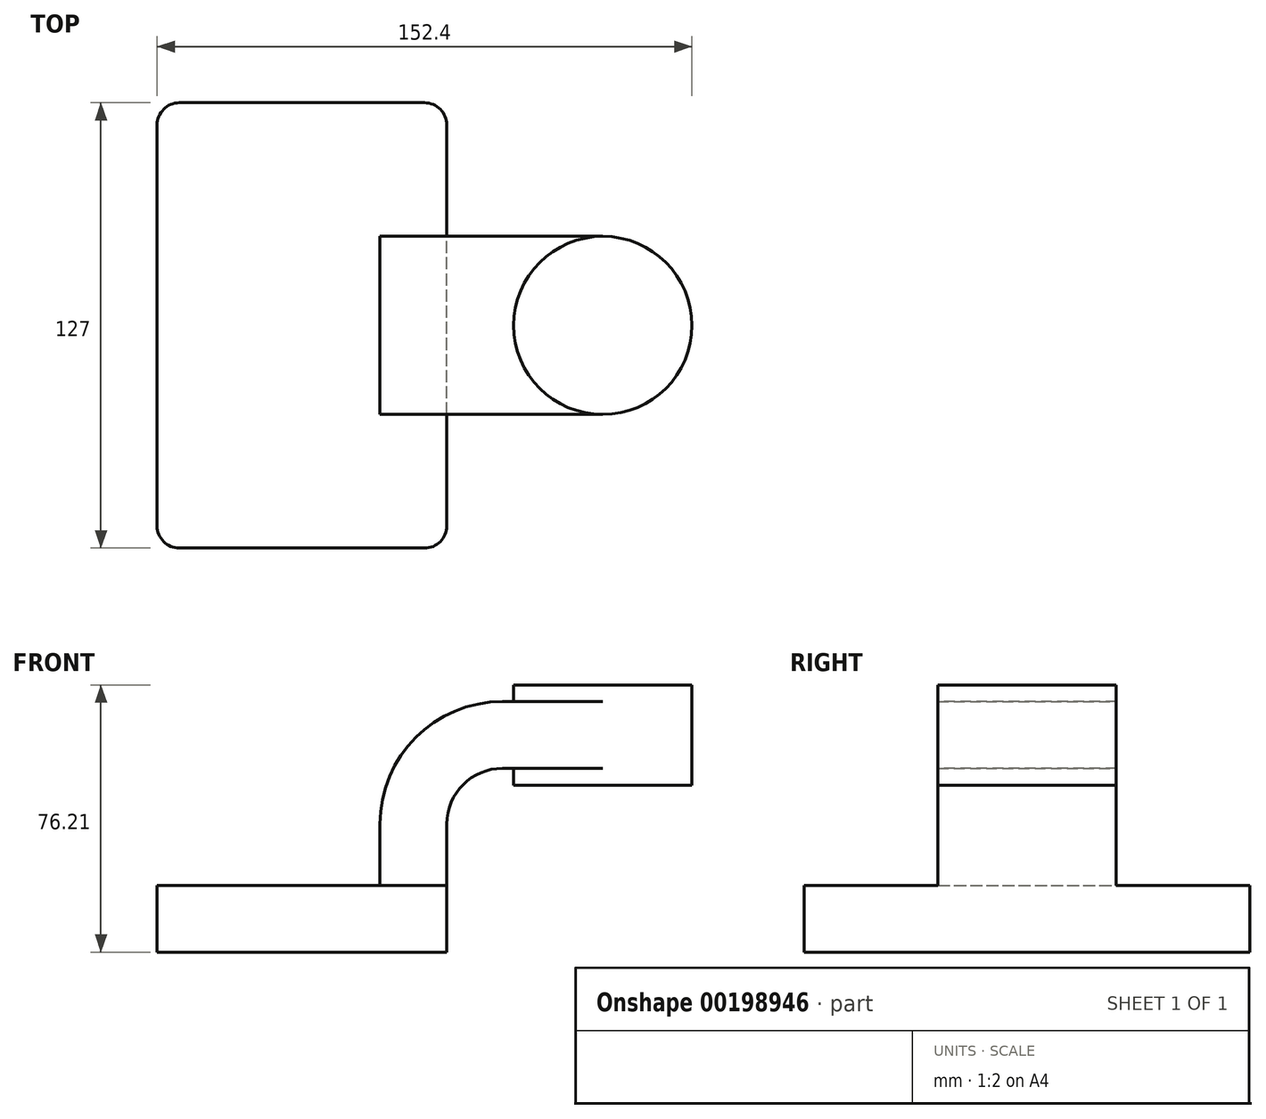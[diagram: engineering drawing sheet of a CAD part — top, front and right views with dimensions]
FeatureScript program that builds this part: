
annotation { "Feature Type Name" : "Feature", "Feature Type Description" : "" }
export const myFeature = defineFeature(function(context is Context, id is Id, definition is map)
    precondition{}
    {
        {
            var Q0;
            Q0=qCreatedBy(makeId("Front.planeOp"),FACE);
            var sketch = newSketch(context, id + "F0", { "sketchPlane" : qUnion([Q0])});
            skLineSegment(sketch, "E0.bottom", {"start": v(-41.28, 9.52) * mm, "end": v(41.28, 9.53) * mm});
            skLineSegment(sketch, "E0.top", {"start": v(-41.28, -9.53) * mm, "end": v(41.28, -9.53) * mm});
            skLineSegment(sketch, "E0.left", {"start": v(-41.28, 9.52) * mm, "end": v(-41.28, -9.53) * mm});
            skLineSegment(sketch, "E0.right", {"start": v(41.28, 9.53) * mm, "end": v(41.28, -9.52) * mm});
            skPoint(sketch, "E0.middle", {"position": v(0, 0) * mm});
            skLineSegment(sketch, "E1.bottom", {"start": v(60.33, 66.67) * mm, "end": v(111.12, 66.67) * mm});
            skLineSegment(sketch, "E1.top", {"start": v(60.33, 38.1) * mm, "end": v(111.12, 38.1) * mm});
            skLineSegment(sketch, "E1.left", {"start": v(60.33, 66.68) * mm, "end": v(60.33, 38.1) * mm});
            skLineSegment(sketch, "E1.right", {"start": v(111.12, 66.67) * mm, "end": v(111.12, 38.1) * mm});
            skPoint(sketch, "E1.middle", {"position": v(85.73, 52.39) * mm});
            skLineSegment(sketch, "E2", {"start": v(41.27, 9.53) * mm, "end": v(41.27, 27) * mm});
            skArc(sketch, "E3", {"start": v(41.27, 27) * mm, "mid": v(45.92, 38.23) * mm, "end": v(57.15, 42.88) * mm});
            skLineSegment(sketch, "E4", {"start": v(57.15, 42.88) * mm, "end": v(85.73, 42.88) * mm});
            skLineSegment(sketch, "E5.0", {"start": v(57.15, 61.93) * mm, "end": v(85.73, 61.93) * mm});
            skArc(sketch, "E5.1", {"start": v(22.22, 27) * mm, "mid": v(32.45, 51.7) * mm, "end": v(57.15, 61.93) * mm});
            skLineSegment(sketch, "E5.2", {"start": v(22.23, 9.53) * mm, "end": v(22.23, 27) * mm});
            skLineSegment(sketch, "E6", {"start": v(85.73, 66.67) * mm, "end": v(85.73, 38.1) * mm});
            skFitSpline(sketch, "E7", {"points": [v(-41.28, 9.52) * mm, v(57.15, 61.93) * mm], "startDerivative": vector(6.55, 94.18) * mm, "endDerivative": vector(106.57, 0) * mm});
            skSolve(sketch);
        }
        {
            var Q0;
            Q0=makeQuery(id+"F0.imprint","IMPRINT",FACE,{"disambiguationData":[TD([[makeQuery(id+"F0.imprint","IMPRINT",EDGE,{"derivedFrom":sQuery(id+"F0.wireOp",EDGE,"E0.top")}),1.0]])]});
            extrude(context, id + "F1", {"entities" : qUnion([Q0]), "endBound" : BoundingType.SYMMETRIC, "depth" : 127 * mm});
        }
        {
            var Q0;
            {var subQ0=sQuery(id+"F0.wireOp",EDGE,"E5.0");var subQ1=sQuery(id+"F0.wireOp",EDGE,"E1.left");var subQ2=makeQuery(id+"F0.imprint","INTERSECT",VERTEX,{"derivedFrom":[subQ1,subQ0]});Q0=makeQuery(id+"F0.imprint","IMPRINT",FACE,{"disambiguationData":[TD([[makeQuery(id+"F0.imprint","IMPRINT",EDGE,{"disambiguationData":[TD([[subQ2,-1.0]])],"derivedFrom":subQ1}),1.0]])]});}
            var Q1;
            {var subQ1=sQuery(id+"F0.wireOp",EDGE,"E2");Q1=makeQuery(id+"F0.imprint","IMPRINT",FACE,{"disambiguationData":[TD([[makeQuery(id+"F0.imprint","IMPRINT",EDGE,{"derivedFrom":subQ1}),1.0]])]});}
            extrude(context, id + "F2", {"entities" : qUnion([Q0, Q1]), "operationType" : NewBodyOperationType.ADD, "endBound" : BoundingType.SYMMETRIC, "depth" : 50.8 * mm});
        }
        {
            var Q0;
            Q0=makeQuery(id+"F0.imprint","IMPRINT",FACE,{"disambiguationData":[TD([[makeQuery(id+"F0.imprint","IMPRINT",EDGE,{"derivedFrom":sQuery(id+"F0.wireOp",EDGE,"E5.1")}),1.0]])]});
            extrude(context, id + "F3", {"entities" : qUnion([Q0]), "operationType" : NewBodyOperationType.ADD, "endBound" : BoundingType.SYMMETRIC, "depth" : 15.88 * mm});
        }
        {
            var Q0;
            {var subQ0=sQuery(id+"F0.wireOp",EDGE,"E1.right");Q0=makeQuery(id+"F0.imprint","IMPRINT",FACE,{"disambiguationData":[TD([[makeQuery(id+"F0.imprint","IMPRINT",EDGE,{"derivedFrom":subQ0}),-1.0]])]});}
            var Q1;
            Q1=sQuery(id+"F0.wireOp",EDGE,"E6");
            revolve(context, id + "F4", {"operationType" : NewBodyOperationType.ADD, "entities" : qUnion([Q0]), "axis" : qUnion([Q1]), "revolveType" : RevolveType.FULL});
        }
        {
            var Q0;
            Q0=makeQuery(id+"F1.opExtrude","CAP_EDGE",EDGE,{"disambiguationData":[OSD([sQuery(id+"F0.wireOp",EDGE,"E0.right")])],"isStart":false});
            var Q1;
            Q1=makeQuery(id+"F1.opExtrude","CAP_EDGE",EDGE,{"disambiguationData":[OSD([sQuery(id+"F0.wireOp",EDGE,"E0.left")])],"isStart":false});
            var Q2;
            Q2=makeQuery(id+"F1.opExtrude","CAP_EDGE",EDGE,{"disambiguationData":[OSD([sQuery(id+"F0.wireOp",EDGE,"E0.right")])],"isStart":true});
            var Q3;
            Q3=makeQuery(id+"F1.opExtrude","CAP_EDGE",EDGE,{"disambiguationData":[OSD([sQuery(id+"F0.wireOp",EDGE,"E0.left")])],"isStart":true});
            fillet(context, id + "F5", {"entities" : qUnion([Q0, Q1, Q2, Q3]), "radius" : 6.35 * mm, "tangentPropagation" : true, "allowEdgeOverflow" : false});
        }
    });
